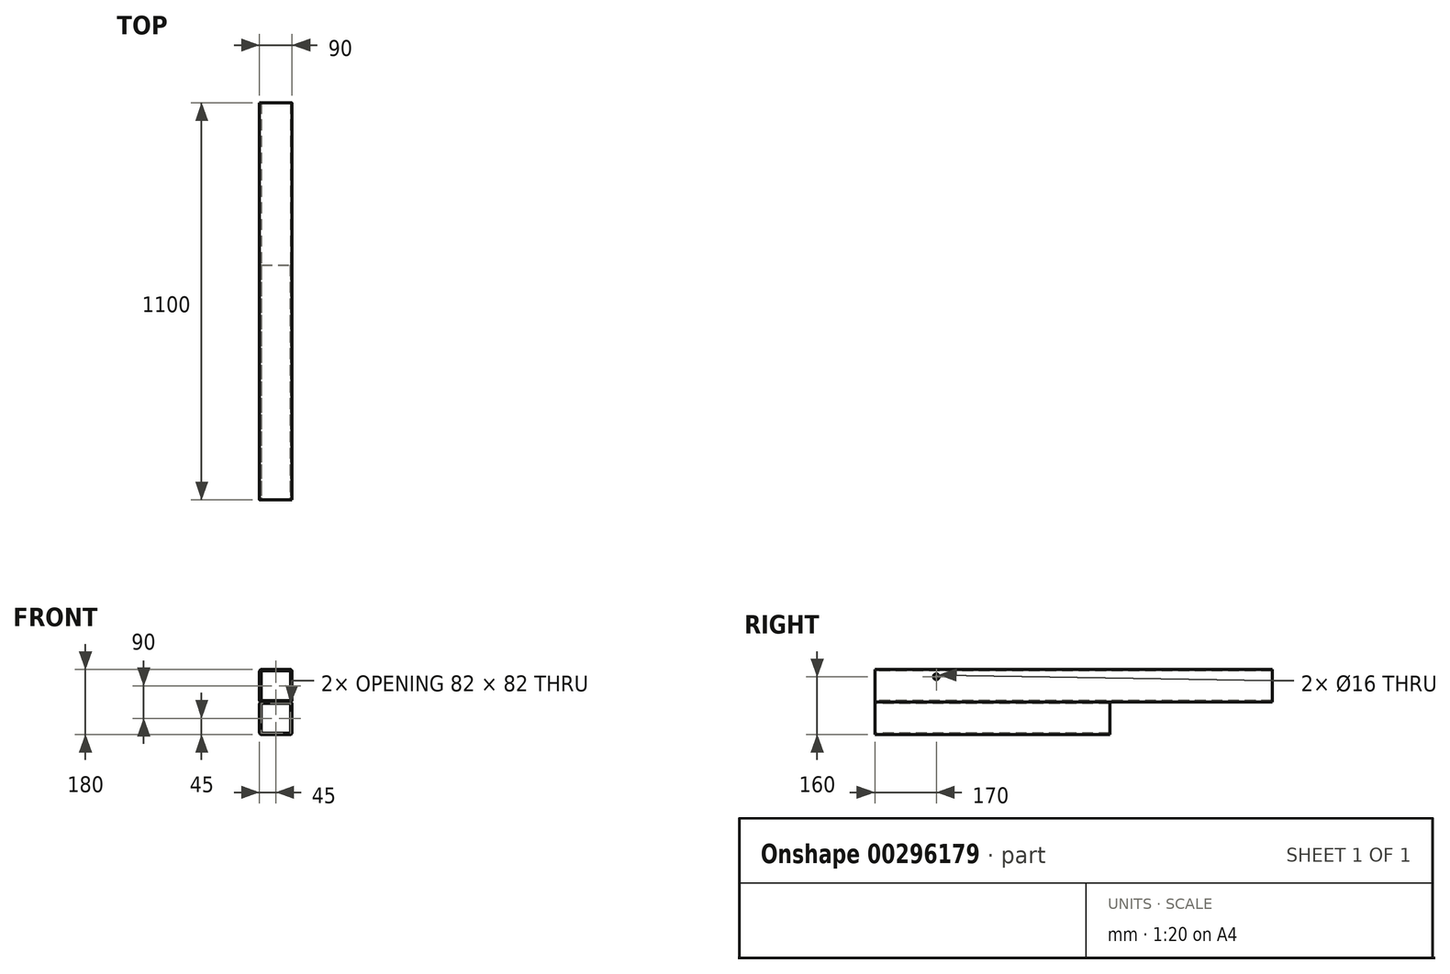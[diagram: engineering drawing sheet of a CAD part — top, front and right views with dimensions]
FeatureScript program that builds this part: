
annotation { "Feature Type Name" : "Feature", "Feature Type Description" : "" }
export const myFeature = defineFeature(function(context is Context, id is Id, definition is map)
    precondition{}
    {
        {
            var Q0;
            Q0=qCreatedBy(makeId("Front.planeOp"),FACE);
            var sketch = newSketch(context, id + "F0", { "sketchPlane" : qUnion([Q0])});
            skLineSegment(sketch, "E0.bottom", {"start": v(40, 45) * mm, "end": v(-40, 45) * mm});
            skLineSegment(sketch, "E0.top", {"start": v(40, -45) * mm, "end": v(-40, -45) * mm});
            skLineSegment(sketch, "E0.left", {"start": v(45, 40) * mm, "end": v(45, -40) * mm});
            skLineSegment(sketch, "E0.right", {"start": v(-45, 40) * mm, "end": v(-45, -40) * mm});
            skPoint(sketch, "E0.middle", {"position": v(0, 0) * mm});
            skPoint(sketch, "E1.visualSharp", {"position": v(-45, 45) * mm});
            skArc(sketch, "E1.filletArc", {"start": v(-40, 45) * mm, "mid": v(-43.54, 43.54) * mm, "end": v(-45, 40) * mm});
            skPoint(sketch, "E2.visualSharp", {"position": v(45, 45) * mm});
            skArc(sketch, "E2.filletArc", {"start": v(45, 40) * mm, "mid": v(43.54, 43.54) * mm, "end": v(40, 45) * mm});
            skPoint(sketch, "E3.visualSharp", {"position": v(45, -45) * mm});
            skArc(sketch, "E3.filletArc", {"start": v(40, -45) * mm, "mid": v(43.54, -43.54) * mm, "end": v(45, -40) * mm});
            skPoint(sketch, "E4.visualSharp", {"position": v(-45, -45) * mm});
            skArc(sketch, "E4.filletArc", {"start": v(-45, -40) * mm, "mid": v(-43.54, -43.54) * mm, "end": v(-40, -45) * mm});
            skArc(sketch, "E5.0", {"start": v(-40, 41) * mm, "mid": v(-40.7, 40.7) * mm, "end": v(-41, 40) * mm});
            skLineSegment(sketch, "E5.1", {"start": v(40, 41) * mm, "end": v(-40, 41) * mm});
            skLineSegment(sketch, "E5.2", {"start": v(-41, 40) * mm, "end": v(-41, -40) * mm});
            skArc(sketch, "E5.3", {"start": v(41, 40) * mm, "mid": v(40.7, 40.7) * mm, "end": v(40, 41) * mm});
            skArc(sketch, "E5.4", {"start": v(-41, -40) * mm, "mid": v(-40.7, -40.7) * mm, "end": v(-40, -41) * mm});
            skLineSegment(sketch, "E5.5", {"start": v(40, -41) * mm, "end": v(-40, -41) * mm});
            skArc(sketch, "E5.6", {"start": v(40, -41) * mm, "mid": v(40.7, -40.7) * mm, "end": v(41, -40) * mm});
            skLineSegment(sketch, "E5.7", {"start": v(41, 40) * mm, "end": v(41, -40) * mm});
            skLineSegment(sketch, "E6.top", {"start": v(40, -135) * mm, "end": v(-40, -135) * mm});
            skLineSegment(sketch, "E6.left", {"start": v(45, -50) * mm, "end": v(45, -130) * mm});
            skLineSegment(sketch, "E6.right", {"start": v(-45, -50) * mm, "end": v(-45, -130) * mm});
            skPoint(sketch, "E6.middle", {"position": v(0, -90) * mm});
            skArc(sketch, "E7.filletArc", {"start": v(-40, -45) * mm, "mid": v(-43.54, -46.46) * mm, "end": v(-45, -50) * mm});
            skArc(sketch, "E8.filletArc", {"start": v(45, -50) * mm, "mid": v(43.54, -46.46) * mm, "end": v(40, -45) * mm});
            skPoint(sketch, "E9.visualSharp", {"position": v(45, -135) * mm});
            skArc(sketch, "E9.filletArc", {"start": v(40, -135) * mm, "mid": v(43.54, -133.54) * mm, "end": v(45, -130) * mm});
            skPoint(sketch, "E10.visualSharp", {"position": v(-45, -135) * mm});
            skArc(sketch, "E10.filletArc", {"start": v(-45, -130) * mm, "mid": v(-43.54, -133.54) * mm, "end": v(-40, -135) * mm});
            skArc(sketch, "E11.0", {"start": v(-40, -49) * mm, "mid": v(-40.7, -49.3) * mm, "end": v(-41, -50) * mm});
            skLineSegment(sketch, "E11.1", {"start": v(40, -49) * mm, "end": v(-40, -49) * mm});
            skLineSegment(sketch, "E11.2", {"start": v(-41, -50) * mm, "end": v(-41, -130) * mm});
            skArc(sketch, "E11.3", {"start": v(41, -50) * mm, "mid": v(40.7, -49.3) * mm, "end": v(40, -49) * mm});
            skArc(sketch, "E11.4", {"start": v(-41, -130) * mm, "mid": v(-40.7, -130.7) * mm, "end": v(-40, -131) * mm});
            skLineSegment(sketch, "E11.5", {"start": v(40, -131) * mm, "end": v(-40, -131) * mm});
            skArc(sketch, "E11.6", {"start": v(40, -131) * mm, "mid": v(40.7, -130.7) * mm, "end": v(41, -130) * mm});
            skLineSegment(sketch, "E11.7", {"start": v(41, -50) * mm, "end": v(41, -130) * mm});
            skSolve(sketch);
        }
        {
            var Q0;
            Q0=makeQuery(id+"F0.imprint","IMPRINT",FACE,{"disambiguationData":[TD([[makeQuery(id+"F0.imprint","IMPRINT",EDGE,{"derivedFrom":sQuery(id+"F0.wireOp",EDGE,"E0.bottom")}),1.0]])]});
            var Q1;
            Q1=makeQuery(id+"F0.imprint","IMPRINT",FACE,{"disambiguationData":[TD([[makeQuery(id+"F0.imprint","IMPRINT",EDGE,{"derivedFrom":sQuery(id+"F0.wireOp",EDGE,"E0.top")}),1.0]])]});
            extrude(context, id + "F1", {"entities" : qUnion([Q0, Q1]), "oppositeDirection" : true, "depth" : 1100 * mm});
        }
        {
            var Q0;
            Q0=makeQuery(id+"F1.opExtrude","SWEPT_FACE",FACE,{"disambiguationData":[OSD([sQuery(id+"F0.wireOp",EDGE,"E0.left")])]});
            var sketch = newSketch(context, id + "F2", { "sketchPlane" : qUnion([Q0])});
            skCircle(sketch, "E12", {"center": v(170, 25) * mm, "radius": 8 * mm});
            skSolve(sketch);
        }
        {
            var Q0;
            Q0=makeQuery(id+"F2.imprint","IMPRINT",FACE,{"disambiguationData":[TD([[makeQuery(id+"F2.imprint","IMPRINT",EDGE,{"derivedFrom":sQuery(id+"F2.wireOp",EDGE,"E12")}),1.0]])]});
            extrude(context, id + "F3", {"entities" : qUnion([Q0]), "operationType" : NewBodyOperationType.REMOVE, "endBound" : BoundingType.THROUGH_ALL, "oppositeDirection" : true, "depth" : 25 * mm});
        }
        {
            var Q0;
            Q0=makeQuery(id+"F1.opExtrude","SWEPT_FACE",FACE,{"disambiguationData":[OSD([sQuery(id+"F0.wireOp",EDGE,"E6.left")])]});
            var sketch = newSketch(context, id + "F4", { "sketchPlane" : qUnion([Q0])});
            skLineSegment(sketch, "E13.bottom", {"start": v(650, -45) * mm, "end": v(1100, -45) * mm});
            skLineSegment(sketch, "E13.top", {"start": v(650, -135) * mm, "end": v(1100, -135) * mm});
            skLineSegment(sketch, "E13.left", {"start": v(650, -45) * mm, "end": v(650, -135) * mm});
            skLineSegment(sketch, "E13.right", {"start": v(1100, -45) * mm, "end": v(1100, -135) * mm});
            skSolve(sketch);
        }
        {
            var Q0;
            {var subQ0=sQuery(id+"F4.wireOp",EDGE,"E13.left");var subQ1=sQuery(id+"F0.wireOp",EDGE,"E6.left");var subQ2=makeQuery(id+"F1.opExtrude","SWEPT_EDGE",EDGE,{"disambiguationData":[OSD([subQ1,sQuery(id+"F0.wireOp",EDGE,"E8.filletArc")])]});var subQ3=makeQuery(id+"F4.imprint","INTERSECT",VERTEX,{"derivedFrom":[subQ2,subQ0]});Q0=makeQuery(id+"F4.imprint","IMPRINT",FACE,{"disambiguationData":[TD([[makeQuery(id+"F4.imprint","IMPRINT",EDGE,{"disambiguationData":[TD([[subQ3,-1.0]])],"derivedFrom":subQ0}),1.0]])]});}
            var Q1;
            {var subQ0=sQuery(id+"F4.wireOp",EDGE,"E13.top");Q1=makeQuery(id+"F4.imprint","IMPRINT",FACE,{"disambiguationData":[TD([[makeQuery(id+"F4.imprint","IMPRINT",EDGE,{"derivedFrom":subQ0}),1.0]])]});}
            var Q2;
            {var subQ0=sQuery(id+"F4.wireOp",EDGE,"E13.bottom");Q2=makeQuery(id+"F4.imprint","IMPRINT",FACE,{"disambiguationData":[TD([[makeQuery(id+"F4.imprint","IMPRINT",EDGE,{"derivedFrom":subQ0}),-1.0]])]});}
            extrude(context, id + "F5", {"entities" : qUnion([Q0, Q1, Q2]), "operationType" : NewBodyOperationType.REMOVE, "endBound" : BoundingType.THROUGH_ALL, "oppositeDirection" : true, "depth" : 25 * mm});
        }
    });
